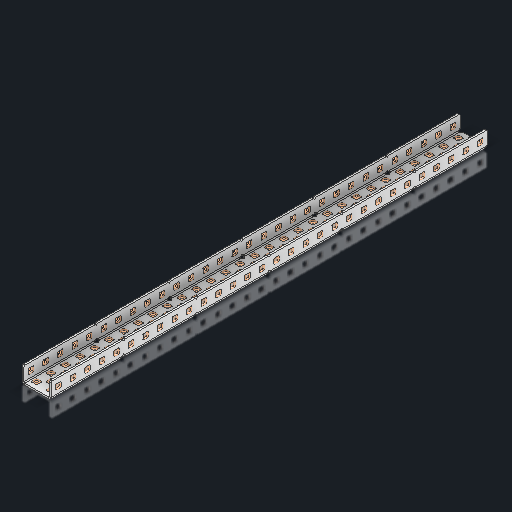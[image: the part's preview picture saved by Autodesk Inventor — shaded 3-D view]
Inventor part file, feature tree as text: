
AUTODESK INVENTOR PART (.ipt)
format: ipt  version: 2023.2 (Build 272271030, 271C)  size: 2,590,208 bytes
history: native  units: in
note: dims shown in document units (in); Inventor stores cm internally (conversion verified against a paired STEP export)
features: other x306, sketch x10, sheet_metal_op x1
ambient origin geometry x8: Origin, YZ Plane, XZ Plane, XY Plane, X Axis, Y Axis, Z Axis, Center Point
bodies: Solid1 (feature_tree)
feature tree (317):
  other  "Alu C 1x2x1x30_MIR.ipt"
  other  "Solid1::Alu C 1x2x1x30_MIR.ipt"
  other  "TaggingFeature1"
  sketch  "Sketch1"  dims[d0=0.3937in]
  sketch  "Sketch2"  dims[d1=0.0625in]
  sketch  "Sketch3"
  sketch  "Sketch7"
  other  "Flange Pattern Sketch"
  sketch  "Sketch8"
  sketch  "Sketch9"
  sheet_metal_op  "Body Pattern Sketch"
  sketch  "Sketch15"
  sketch  "Sketch16"
  other  "Arc Length"
  sketch  "Sketch13"
  sketch  "Sketch14"
  other  "Flange Pattern Plane"
  other  "Srf1"
  other  "Srf2"
  other  "Srf3"
  other  "Srf4"
  other  "Srf5"
  other  "Srf6"
  other  "Srf7"
  other  "Srf8"
  other  "Srf9"
  other  "Srf10"
  other  "Srf11"
  other  "Srf12"
  other  "Srf13"
  other  "Srf14"
  other  "Srf15"
  other  "Srf16"
  other  "Srf17"
  other  "Srf18"
  other  "Srf19"
  other  "Srf20"
  other  "Srf21"
  other  "Srf22"
  other  "Srf23"
  other  "Srf24"
  other  "Srf25"
  other  "Srf26"
  other  "Srf27"
  other  "Srf28"
  other  "Srf29"
  other  "Srf30"
  other  "Srf31"
  other  "Srf32"
  other  "Srf33"
  other  "Srf34"
  other  "Srf35"
  other  "Srf36"
  other  "Srf37"
  other  "Srf38"
  other  "Srf39"
  other  "Srf40"
  other  "Srf41"
  other  "Srf42"
  other  "Srf43"
  other  "Srf44"
  other  "Srf45"
  other  "Srf46"
  other  "Srf47"
  other  "Srf48"
  other  "Srf49"
  other  "Srf50"
  other  "Srf51"
  other  "Srf52"
  other  "Srf53"
  other  "Srf54"
  other  "Srf55"
  other  "Srf56"
  other  "Srf57"
  other  "Srf58"
  other  "Srf59"
  other  "Srf60"
  other  "Srf61"
  other  "Srf62"
  other  "Srf63"
  other  "Srf64"
  other  "Srf65"
  other  "Srf66"
  other  "Srf67"
  other  "Srf68"
  other  "Srf69"
  other  "Srf70"
  other  "Srf71"
  other  "Srf72"
  other  "Srf73"
  other  "Srf74"
  other  "Srf75"
  other  "Srf76"
  other  "Srf77"
  other  "Srf78"
  other  "Srf79"
  other  "Srf80"
  other  "Srf81"
  other  "Srf82"
  other  "Srf83"
  other  "Srf84"
  other  "Srf85"
  other  "Srf86"
  other  "Srf87"
  other  "Srf88"
  other  "Srf89"
  other  "Srf90"
  other  "Srf91"
  other  "Srf92"
  other  "Srf93"
  other  "Srf94"
  other  "Srf95"
  other  "Srf96"
  other  "Srf97"
  other  "Srf98"
  other  "Srf99"
  other  "Srf100"
  other  "Srf101"
  other  "Srf102"
  other  "Srf103"
  other  "Srf104"
  other  "Srf105"
  other  "Srf106"
  other  "Srf107"
  other  "Srf108"
  other  "Srf109"
  other  "Srf110"
  other  "Srf111"
  other  "Srf112"
  other  "Srf113"
  other  "Srf114"
  other  "Srf115"
  other  "Srf116"
  other  "Srf117"
  other  "Srf118"
  other  "Srf119"
  other  "Srf120"
  other  "Srf121"
  other  "Srf122"
  other  "Srf123"
  other  "Srf124"
  other  "Srf125"
  other  "Srf126"
  other  "Srf127"
  other  "Srf128"
  other  "Srf129"
  other  "Srf130"
  other  "Srf131"
  other  "Srf132"
  other  "Srf133"
  other  "Srf134"
  other  "Srf135"
  other  "Srf136"
  other  "Srf137"
  other  "Srf138"
  other  "Srf139"
  other  "Srf140"
  other  "Srf141"
  other  "Srf142"
  other  "Srf143"
  other  "Srf144"
  other  "Srf145"
  other  "Srf146"
  other  "Srf147"
  other  "Srf148"
  other  "Srf149"
  other  "Srf150"
  other  "Srf1::Derived"
  other  "Srf2::Derived"
  other  "Srf3::Derived"
  other  "Srf4::Derived"
  other  "Srf5::Derived"
  other  "Srf6::Derived"
  other  "Srf7::Derived"
  other  "Srf8::Derived"
  other  "Srf9::Derived"
  other  "Srf10::Derived"
  other  "Srf11::Derived"
  other  "Srf12::Derived"
  other  "Srf13::Derived"
  other  "Srf14::Derived"
  other  "Srf15::Derived"
  other  "Srf16::Derived"
  other  "Srf17::Derived"
  other  "Srf18::Derived"
  other  "Srf19::Derived"
  other  "Srf20::Derived"
  other  "Srf21::Derived"
  other  "Srf22::Derived"
  other  "Srf23::Derived"
  other  "Srf24::Derived"
  other  "Srf25::Derived"
  other  "Srf26::Derived"
  other  "Srf27::Derived"
  other  "Srf28::Derived"
  other  "Srf29::Derived"
  other  "Srf30::Derived"
  other  "Srf31::Derived"
  other  "Srf32::Derived"
  other  "Srf33::Derived"
  other  "Srf34::Derived"
  other  "Srf35::Derived"
  other  "Srf36::Derived"
  other  "Srf37::Derived"
  other  "Srf38::Derived"
  other  "Srf39::Derived"
  other  "Srf40::Derived"
  other  "Srf41::Derived"
  other  "Srf42::Derived"
  other  "Srf43::Derived"
  other  "Srf44::Derived"
  other  "Srf45::Derived"
  other  "Srf46::Derived"
  other  "Srf47::Derived"
  other  "Srf48::Derived"
  other  "Srf49::Derived"
  other  "Srf50::Derived"
  other  "Srf51::Derived"
  other  "Srf52::Derived"
  other  "Srf53::Derived"
  other  "Srf54::Derived"
  other  "Srf55::Derived"
  other  "Srf56::Derived"
  other  "Srf57::Derived"
  other  "Srf58::Derived"
  other  "Srf59::Derived"
  other  "Srf60::Derived"
  other  "Srf61::Derived"
  other  "Srf62::Derived"
  other  "Srf63::Derived"
  other  "Srf64::Derived"
  other  "Srf65::Derived"
  other  "Srf66::Derived"
  other  "Srf67::Derived"
  other  "Srf68::Derived"
  other  "Srf69::Derived"
  other  "Srf70::Derived"
  other  "Srf71::Derived"
  other  "Srf72::Derived"
  other  "Srf73::Derived"
  other  "Srf74::Derived"
  other  "Srf75::Derived"
  other  "Srf76::Derived"
  other  "Srf77::Derived"
  other  "Srf78::Derived"
  other  "Srf79::Derived"
  other  "Srf80::Derived"
  other  "Srf81::Derived"
  other  "Srf82::Derived"
  other  "Srf83::Derived"
  other  "Srf84::Derived"
  other  "Srf85::Derived"
  other  "Srf86::Derived"
  other  "Srf87::Derived"
  other  "Srf88::Derived"
  other  "Srf89::Derived"
  other  "Srf90::Derived"
  other  "Srf91::Derived"
  other  "Srf92::Derived"
  other  "Srf93::Derived"
  other  "Srf94::Derived"
  other  "Srf95::Derived"
  other  "Srf96::Derived"
  other  "Srf97::Derived"
  other  "Srf98::Derived"
  other  "Srf99::Derived"
  other  "Srf100::Derived"
  other  "Srf101::Derived"
  other  "Srf102::Derived"
  other  "Srf103::Derived"
  other  "Srf104::Derived"
  other  "Srf105::Derived"
  other  "Srf106::Derived"
  other  "Srf107::Derived"
  other  "Srf108::Derived"
  other  "Srf109::Derived"
  other  "Srf110::Derived"
  other  "Srf111::Derived"
  other  "Srf112::Derived"
  other  "Srf113::Derived"
  other  "Srf114::Derived"
  other  "Srf115::Derived"
  other  "Srf116::Derived"
  other  "Srf117::Derived"
  other  "Srf118::Derived"
  other  "Srf119::Derived"
  other  "Srf120::Derived"
  other  "Srf121::Derived"
  other  "Srf122::Derived"
  other  "Srf123::Derived"
  other  "Srf124::Derived"
  other  "Srf125::Derived"
  other  "Srf126::Derived"
  other  "Srf127::Derived"
  other  "Srf128::Derived"
  other  "Srf129::Derived"
  other  "Srf130::Derived"
  other  "Srf131::Derived"
  other  "Srf132::Derived"
  other  "Srf133::Derived"
  other  "Srf134::Derived"
  other  "Srf135::Derived"
  other  "Srf136::Derived"
  other  "Srf137::Derived"
  other  "Srf138::Derived"
  other  "Srf139::Derived"
  other  "Srf140::Derived"
  other  "Srf141::Derived"
  other  "Srf142::Derived"
  other  "Srf143::Derived"
  other  "Srf144::Derived"
  other  "Srf145::Derived"
  other  "Srf146::Derived"
  other  "Srf147::Derived"
  other  "Srf148::Derived"
  other  "Srf149::Derived"
  other  "Srf150::Derived"
